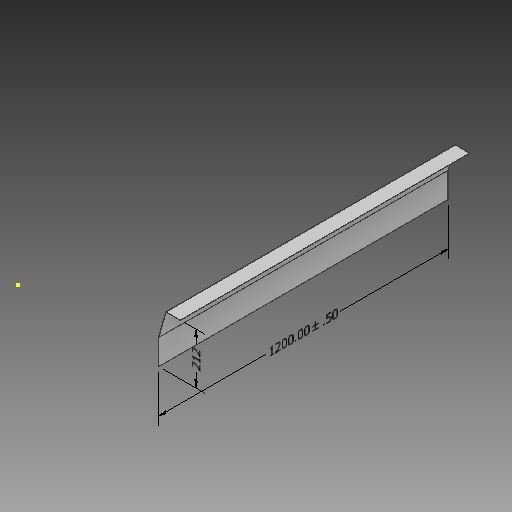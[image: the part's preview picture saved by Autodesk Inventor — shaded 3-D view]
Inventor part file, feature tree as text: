
AUTODESK INVENTOR PART (.ipt)
format: ipt  version: 2018 (Build 220112000, 112)  size: 113,152 bytes
history: native  units: mm
features: other x6, sketch x3, reference x2, extrude x1
ambient origin geometry x8: Origin, YZ Plane, XZ Plane, XY Plane, X Axis, Y Axis, Z Axis, Center Point
bodies: Solid1 (feature_tree)
feature tree (12):
  other  "Annotations"
  sketch  "Sketch1"  dims[d3=1200.0mm d4=0.0mm d5=1200.0mm d6=212.068144mm]
  extrude  "Extrusion1"  Depth=1200.0mm
  sketch  "Sketch3"
  reference  "Reference1"
  reference  "Reference2"
  sketch  "Sketch2"
  other  "Lathe Model 2018.iam"
  other  "Right Leg:1"
  other  "polycarbonate cover:1"
  other  "Linear Dimension 1"
  other  "Linear Dimension 2"
